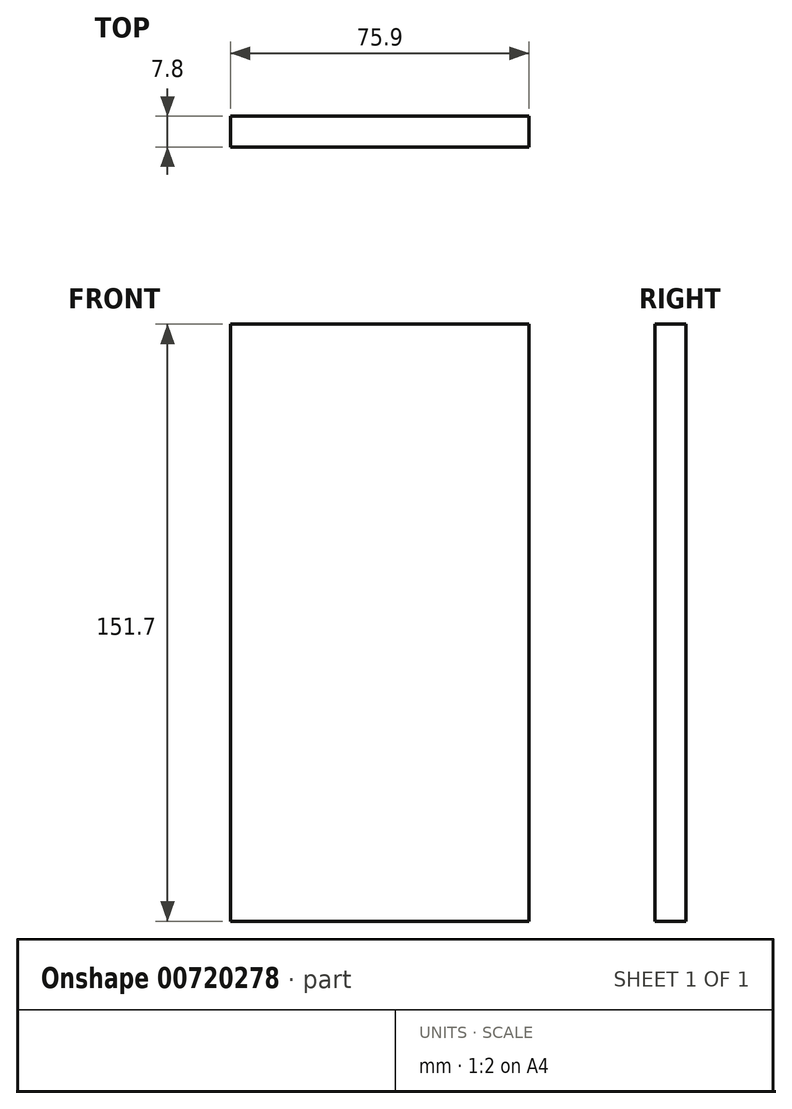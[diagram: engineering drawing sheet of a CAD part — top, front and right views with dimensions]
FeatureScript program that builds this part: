
annotation { "Feature Type Name" : "Feature", "Feature Type Description" : "" }
export const myFeature = defineFeature(function(context is Context, id is Id, definition is map)
    precondition{}
    {
        {
            var Q0;
            Q0=qCreatedBy(makeId("Front.planeOp"),FACE);
            var sketch = newSketch(context, id + "F0", { "sketchPlane" : qUnion([Q0])});
            skLineSegment(sketch, "E0.bottom", {"start": v(37.95, 75.85) * mm, "end": v(-37.95, 75.85) * mm});
            skLineSegment(sketch, "E0.top", {"start": v(37.95, -75.85) * mm, "end": v(-37.95, -75.85) * mm});
            skLineSegment(sketch, "E0.left", {"start": v(37.95, 75.85) * mm, "end": v(37.95, -75.85) * mm});
            skLineSegment(sketch, "E0.right", {"start": v(-37.95, 75.85) * mm, "end": v(-37.95, -75.85) * mm});
            skPoint(sketch, "E0.middle", {"position": v(0, 0) * mm});
            skSolve(sketch);
        }
        {
            var Q0;
            Q0=makeQuery(id+"F0.imprint","IMPRINT",FACE,{"disambiguationData":[TD([[makeQuery(id+"F0.imprint","IMPRINT",EDGE,{"derivedFrom":sQuery(id+"F0.wireOp",EDGE,"E0.bottom")}),1.0]])]});
            extrude(context, id + "F1", {"entities" : qUnion([Q0]), "depth" : 7.8 * mm, "symmetric" : true});
        }
    });
